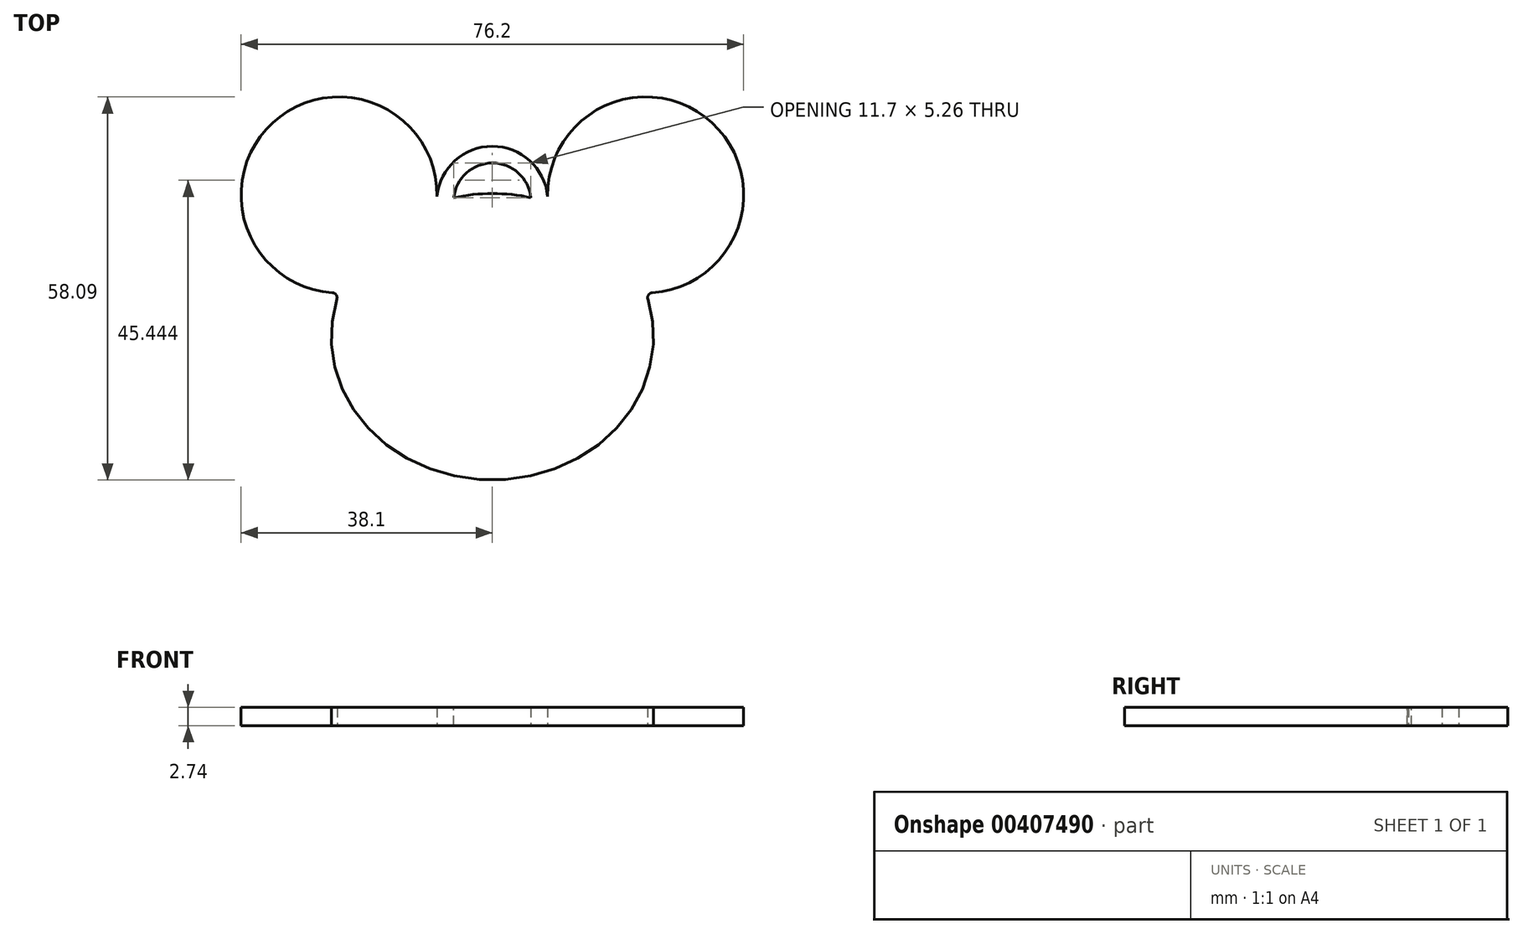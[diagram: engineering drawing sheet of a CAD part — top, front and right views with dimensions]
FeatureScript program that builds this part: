
annotation { "Feature Type Name" : "Feature", "Feature Type Description" : "" }
export const myFeature = defineFeature(function(context is Context, id is Id, definition is map)
    precondition{}
    {
        {
            var Q0;
            Q0=qCreatedBy(makeId("Top.planeOp"),FACE);
            var sketch = newSketch(context, id + "F0", { "sketchPlane" : qUnion([Q0])});
            skEllipticalArc(sketch, "E0", {});
            skArc(sketch, "E1", {"start": v(-8.42, 20.4) * mm, "mid": v(-33.34, 32.42) * mm, "end": v(-23.26, 6.65) * mm});
            skArc(sketch, "E2", {"start": v(23.26, 6.65) * mm, "mid": v(33.34, 32.42) * mm, "end": v(8.42, 20.4) * mm});
            skLineSegment(sketch, "E3", {"start": v(0, 31.6) * mm, "end": v(0, -37.98) * mm, "construction": true});
            skEllipticalArc(sketch, "E4.trimOffspring", {});
            const initialGuessF0  = {"E0": [0, 0, 1, 0, 0.02443560566470645, 0.021722914566711583, 2.830258236929614, 0.31133441666017947], "E4.trimOffspring": [0, 0, 1, 0, 0.02443560566470645, 0.021722914566711583, 1.2188651396096564, 1.9227275139801359]};
            skSetInitialGuess(sketch, initialGuessF0);
            skSolve(sketch);
        }
        {
            var Q0;
            Q0=makeQuery(id+"F0.imprint","IMPRINT",FACE,{"disambiguationData":[TD([[makeQuery(id+"F0.imprint","IMPRINT",EDGE,{"derivedFrom":sQuery(id+"F0.wireOp",EDGE,"E0")}),1.0]])]});
            extrude(context, id + "F1", {"entities" : qUnion([Q0]), "endBound" : BoundingType.SYMMETRIC, "depth" : 2.74 * mm});
        }
        {
            var Q0;
            Q0=qCreatedBy(makeId("Top.planeOp"),FACE);
            var sketch = newSketch(context, id + "F2", { "sketchPlane" : qUnion([Q0])});
            skEllipticalArc(sketch, "E5.0", {});
            skArc(sketch, "E6", {"start": v(8.42, 20.4) * mm, "mid": v(0, 28.9) * mm, "end": v(-8.42, 20.4) * mm});
            skArc(sketch, "E7.0", {"start": v(5.88, 20.42) * mm, "mid": v(0, 26.36) * mm, "end": v(-5.88, 20.42) * mm});
            skLineSegment(sketch, "E8", {"start": v(-8.42, 20.4) * mm, "end": v(-5.88, 20.42) * mm});
            skLineSegment(sketch, "E9", {"start": v(8.42, 20.4) * mm, "end": v(5.88, 20.42) * mm});
            const initialGuessF2  = {"E5.0": [0, 0, 1, 0, 0.02443560566470645, 0.021722914566711583, 1.2188651396096564, 1.9227275139801359]};
            skSetInitialGuess(sketch, initialGuessF2);
            skSolve(sketch);
        }
        {
            var Q0;
            {var subQ0=sQuery(id+"F2.wireOp",EDGE,"E6");Q0=makeQuery(id+"F2.imprint","IMPRINT",FACE,{"disambiguationData":[TD([[makeQuery(id+"F2.imprint","IMPRINT",EDGE,{"derivedFrom":subQ0}),1.0]])]});}
            var Q1;
            Q1=makeQuery(id+"F1.opExtrude","CAP_FACE",FACE,{"disambiguationData":[OSD([sQuery(id+"F0.wireOp",EDGE,"E0"),sQuery(id+"F0.wireOp",EDGE,"E1"),sQuery(id+"F0.wireOp",EDGE,"E2"),sQuery(id+"F0.wireOp",EDGE,"E4.trimOffspring")])],"isStart":false});
            var Q2;
            Q2=makeQuery(id+"F1.opExtrude","CAP_FACE",FACE,{"disambiguationData":[OSD([sQuery(id+"F0.wireOp",EDGE,"E0"),sQuery(id+"F0.wireOp",EDGE,"E1"),sQuery(id+"F0.wireOp",EDGE,"E2"),sQuery(id+"F0.wireOp",EDGE,"E4.trimOffspring")])],"isStart":true});
            extrude(context, id + "F3", {"entities" : qUnion([Q0]), "operationType" : NewBodyOperationType.ADD, "endBound" : BoundingType.UP_TO_SURFACE, "endBoundEntityFace" : qUnion([Q1]), "depth" : 3.8 * mm, "hasSecondDirection" : true, "secondDirectionBound" : SecondDirectionBoundingType.UP_TO_SURFACE, "secondDirectionOppositeDirection" : true, "secondDirectionBoundEntityFace" : qUnion([Q2]), "secondDirectionDepth" : 25.4 * mm});
        }
        {
            var Q0;
            Q0=makeQuery(id+"F3.boolean.opBoolean","INTERSECT",EDGE,{"derivedFrom":[makeQuery(id+"F1.opExtrude","SWEPT_FACE",FACE,{"disambiguationData":[OSD([sQuery(id+"F0.wireOp",EDGE,"E1")])]}),makeQuery(id+"F3.opExtrude","SWEPT_FACE",FACE,{"disambiguationData":[OSD([sQuery(id+"F2.wireOp",EDGE,"y8iNMJ6s-B6sb-voCL-V4kW-FdwGVx5X24oj")])]})]});
            var Q1;
            Q1=makeQuery(id+"F3.boolean.opBoolean","INTERSECT",EDGE,{"derivedFrom":[makeQuery(id+"F1.opExtrude","SWEPT_FACE",FACE,{"disambiguationData":[OSD([sQuery(id+"F0.wireOp",EDGE,"E2")])]}),makeQuery(id+"F3.opExtrude","SWEPT_FACE",FACE,{"disambiguationData":[OSD([sQuery(id+"F2.wireOp",EDGE,"y8iNMJ6s-B6sb-voCL-V4kW-FdwGVx5X24oj")])]})]});
            var Q2;
            {var subQ0=sQuery(id+"F2.wireOp",EDGE,"E7.0");var subQ1=sQuery(id+"F2.wireOp",EDGE,"E5.0");var subQ2=makeQuery(id+"F2.imprint","INTERSECT",VERTEX,{"disambiguationData":[OD(1.0)],"derivedFrom":[subQ1,subQ0]});Q2=makeQuery(id+"F3.opExtrude","TWEAK_EDGE",EDGE,{"derivedFrom":[makeQuery(id+"F2.imprint","IMPRINT",EDGE,{"disambiguationData":[TD([[subQ2,-1.0]])],"derivedFrom":subQ1}),makeQuery(id+"F2.imprint","IMPRINT",EDGE,{"disambiguationData":[TD([[makeQuery(id+"F2.imprint","INTERSECT",VERTEX,{"disambiguationData":[OD(0.0)],"derivedFrom":[subQ1,subQ0]}),-1.0]])],"derivedFrom":subQ0})]});}
            var Q3;
            {var subQ0=sQuery(id+"F2.wireOp",EDGE,"E7.0");var subQ1=sQuery(id+"F2.wireOp",EDGE,"E5.0");var subQ2=makeQuery(id+"F2.imprint","INTERSECT",VERTEX,{"disambiguationData":[OD(0.0)],"derivedFrom":[subQ1,subQ0]});Q3=makeQuery(id+"F3.opExtrude","TWEAK_EDGE",EDGE,{"derivedFrom":[makeQuery(id+"F2.imprint","IMPRINT",EDGE,{"disambiguationData":[TD([[subQ2,1.0]])],"derivedFrom":subQ1}),makeQuery(id+"F2.imprint","IMPRINT",EDGE,{"disambiguationData":[TD([[subQ2,-1.0]])],"derivedFrom":subQ0})]});}
            var Q4;
            Q4=makeQuery(id+"F1.opExtrude","SWEPT_EDGE",EDGE,{"disambiguationData":[OSD([sQuery(id+"F0.wireOp",EDGE,"E0"),sQuery(id+"F0.wireOp",EDGE,"E2")])]});
            var Q5;
            Q5=makeQuery(id+"F1.opExtrude","SWEPT_EDGE",EDGE,{"disambiguationData":[OSD([sQuery(id+"F0.wireOp",EDGE,"E0"),sQuery(id+"F0.wireOp",EDGE,"E1")])]});
            fillet(context, id + "F4", {"entities" : qUnion([Q0, Q1, Q2, Q3, Q4, Q5]), "radius" : 0.76 * mm, "tangentPropagation" : true, "allowEdgeOverflow" : false});
        }
    });
